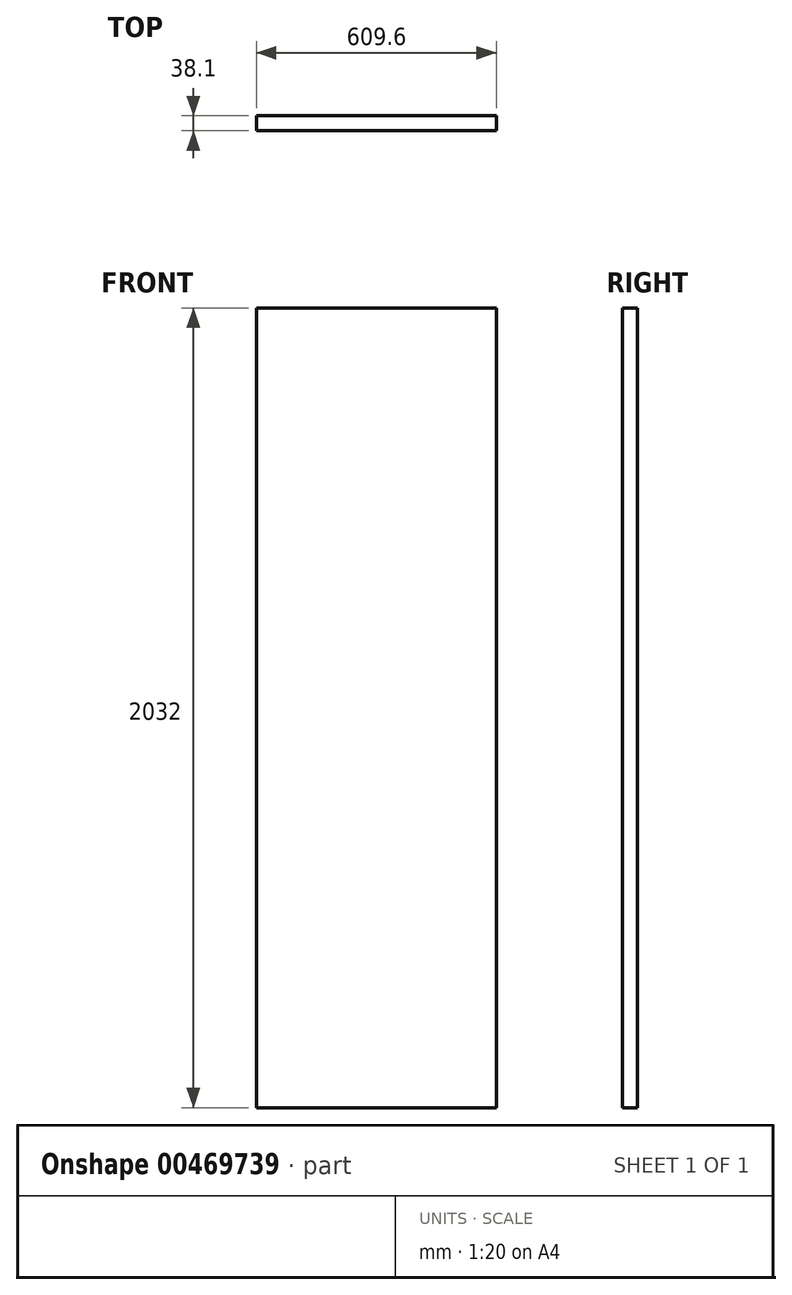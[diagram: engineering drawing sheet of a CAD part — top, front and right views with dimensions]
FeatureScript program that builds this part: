
annotation { "Feature Type Name" : "Feature", "Feature Type Description" : "" }
export const myFeature = defineFeature(function(context is Context, id is Id, definition is map)
    precondition{}
    {
        {
            var Q0;
            Q0=qCreatedBy(makeId("Front.planeOp"),FACE);
            var sketch = newSketch(context, id + "F0", { "sketchPlane" : qUnion([Q0])});
            skLineSegment(sketch, "E0.bottom", {"start": v(0, 0) * mm, "end": v(609.6, 0) * mm});
            skLineSegment(sketch, "E0.top", {"start": v(0, 2032) * mm, "end": v(609.6, 2032) * mm});
            skLineSegment(sketch, "E0.left", {"start": v(0, 0) * mm, "end": v(0, 2032) * mm});
            skLineSegment(sketch, "E0.right", {"start": v(609.6, 0) * mm, "end": v(609.6, 2032) * mm});
            skSolve(sketch);
        }
        {
            var Q0;
            Q0=makeQuery(id+"F0.imprint","IMPRINT",FACE,{"disambiguationData":[TD([[makeQuery(id+"F0.imprint","IMPRINT",EDGE,{"derivedFrom":sQuery(id+"F0.wireOp",EDGE,"E0.bottom")}),1.0]])]});
            extrude(context, id + "F1", {"entities" : qUnion([Q0]), "depth" : 38.1 * mm, "offsetDistance" : 25.4 * mm});
        }
    });
